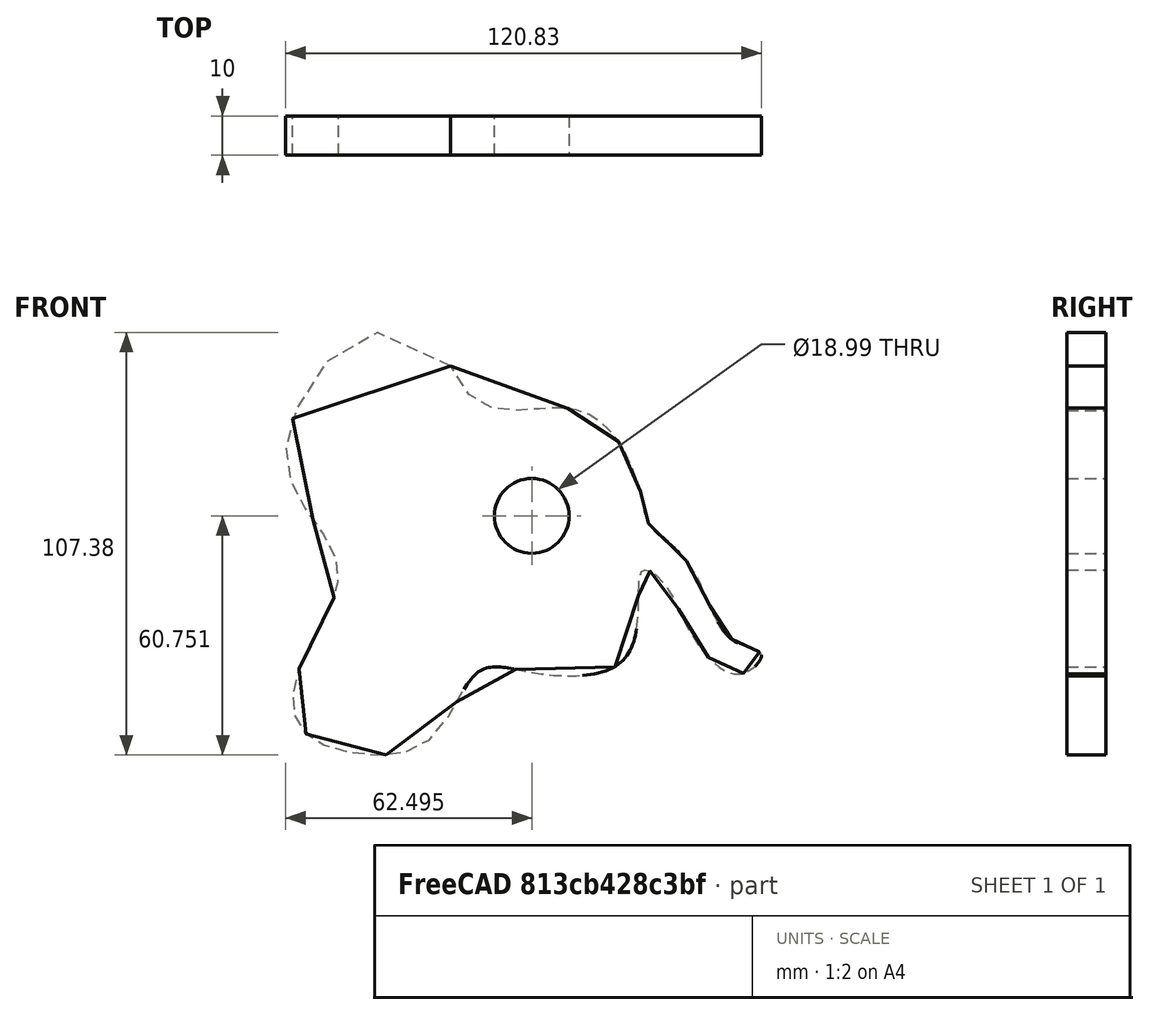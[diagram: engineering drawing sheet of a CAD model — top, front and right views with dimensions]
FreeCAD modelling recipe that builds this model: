
FCSTD DOCUMENT  (FreeCAD 0.20R29410 (Git))
Label: or+t final
License: All rights reserved
LicenseURL: http://en.wikipedia.org/wiki/All_rights_reserved
objects: Sketcher::SketchObject×1, PartDesign::Pad×1, PartDesign::Body×1
note: 4 computed .brp shape members not serialized (recipe doc carries the construction recipe); baked Part::Feature solids carry a one-line shape summary decoded from their .brp

FEATURE [Sketcher::SketchObject] Sketch
  FullyConstrained = false
  MapMode = 5
  Placement = pos=(0,0,0) rot=(1,0,0;1.5708rad)
  Support = -> [XZ_Plane]
  sketch-geometry (62):
    g0-g30: Circle x31 (B-spline internal-alignment scaffolding for g31; pole/knot coordinates omitted)
    g31: BSplineCurve PolesCount=31 KnotsCount=29 Degree=3 IsPeriodic=0
    g32-g60: GeomPoint x29 (B-spline internal-alignment scaffolding for g31; pole/knot coordinates omitted)
    g61: Circle CenterX=-3.87476 CenterY=69.7911 CenterZ=0 NormalX=0 NormalY=0 NormalZ=1 AngleXU=0 Radius=9.49294
  constraints (5):
    c: Weight(g0) = 1
    c: Equal(g0, g1-g30) x30
    c: InternalAlignment(g0-g30 -> g31) x31
    c: InternalAlignment(g32-g60 -> g31) x29
    c: Coincident(g31,g31)
FEATURE [PartDesign::Pad] Pad
  Direction = (0,-1,2e-16)
  Length = 10
  Length2 = 10
  Placement = pos=(0,0,0) rot=(1,0,0;1.5708rad)
  Profile = -> Sketch
  ReferenceAxis = -> Sketch [N_Axis]
  Type = 0
FEATURE [PartDesign::Body] Body
  Group = -> [Sketch,Pad]
  Origin = -> Origin
  Tip = -> Pad
